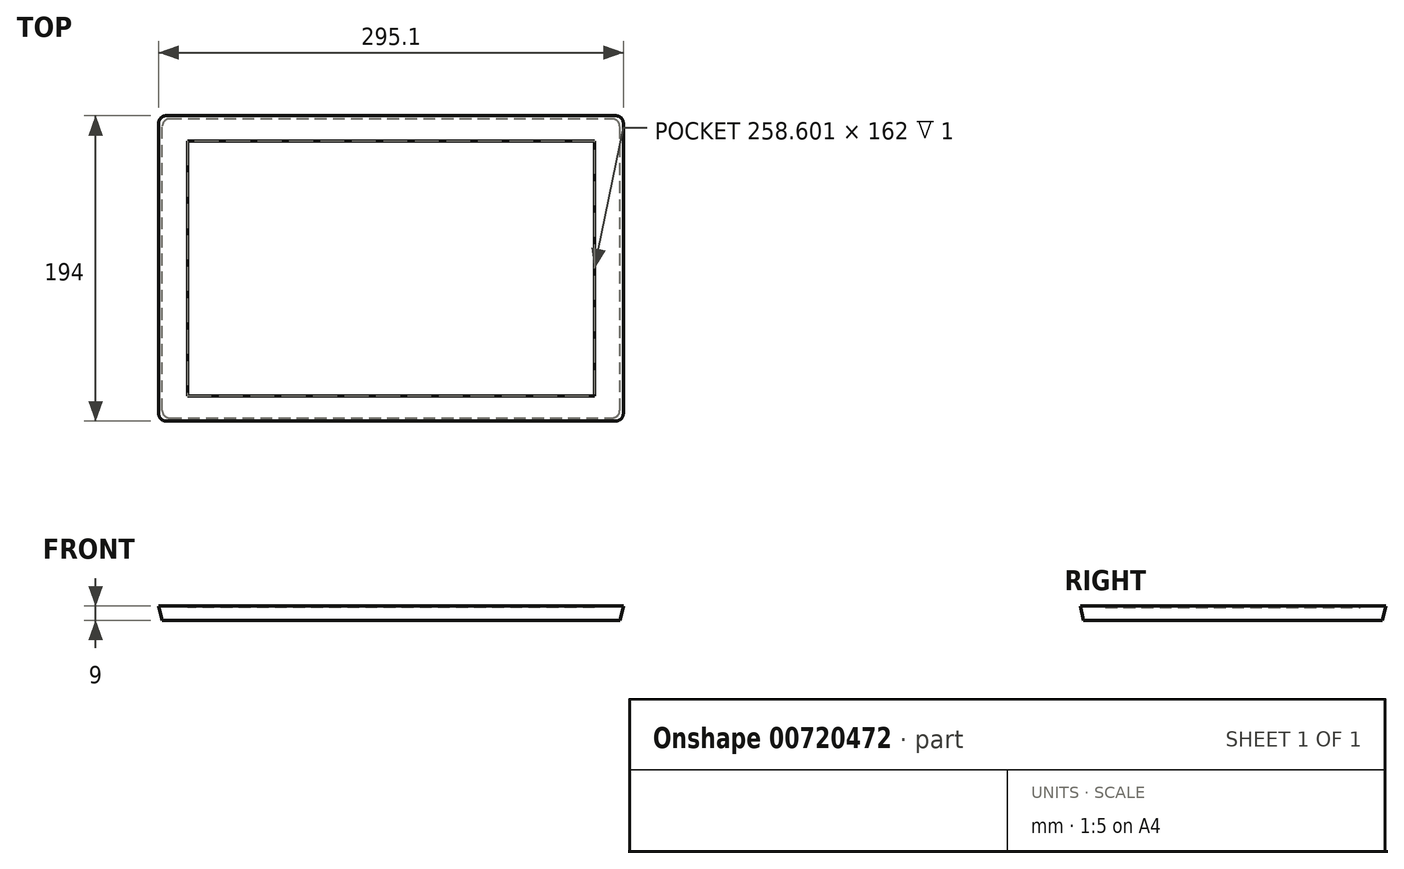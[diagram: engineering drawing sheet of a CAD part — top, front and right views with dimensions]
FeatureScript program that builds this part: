
annotation { "Feature Type Name" : "Feature", "Feature Type Description" : "" }
export const myFeature = defineFeature(function(context is Context, id is Id, definition is map)
    precondition{}
    {
        {
            var Q0;
            Q0=qCreatedBy(makeId("Top.planeOp"),FACE);
            var sketch = newSketch(context, id + "F0", { "sketchPlane" : qUnion([Q0])});
            skLineSegment(sketch, "E0.bottom", {"start": v(141, -97) * mm, "end": v(-141, -97) * mm});
            skLineSegment(sketch, "E0.top", {"start": v(141, 97) * mm, "end": v(-141, 97) * mm});
            skLineSegment(sketch, "E0.left", {"start": v(147.55, -92) * mm, "end": v(147.55, 99) * mm});
            skLineSegment(sketch, "E0.right", {"start": v(-147.55, -92) * mm, "end": v(-147.55, 99) * mm});
            skPoint(sketch, "E0.middle", {"position": v(0, 0) * mm});
            skLineSegment(sketch, "E1.bottom", {"start": v(138.75, -95) * mm, "end": v(-138.75, -95) * mm});
            skLineSegment(sketch, "E1.top", {"start": v(138.75, 95) * mm, "end": v(-138.75, 95) * mm});
            skLineSegment(sketch, "E1.left", {"start": v(145.3, -90) * mm, "end": v(145.3, 97) * mm});
            skLineSegment(sketch, "E1.right", {"start": v(-145.3, -90) * mm, "end": v(-145.3, 97) * mm});
            skLineSegment(sketch, "E2", {"start": v(-145.3, 95) * mm, "end": v(-145.3, 97) * mm});
            skLineSegment(sketch, "E3", {"start": v(-145.3, 95) * mm, "end": v(-138.75, 95) * mm});
            skLineSegment(sketch, "E4", {"start": v(-141, 97) * mm, "end": v(-147.55, 97) * mm});
            skLineSegment(sketch, "E5", {"start": v(-147.55, 99) * mm, "end": v(-147.55, 97) * mm});
            skLineSegment(sketch, "E6", {"start": v(-147.55, -92) * mm, "end": v(-147.55, -97) * mm});
            skLineSegment(sketch, "E7", {"start": v(-147.55, -97) * mm, "end": v(-141, -97) * mm});
            skLineSegment(sketch, "E8", {"start": v(-138.75, -95) * mm, "end": v(-145.3, -95) * mm});
            skLineSegment(sketch, "E9", {"start": v(-145.3, -95) * mm, "end": v(-145.3, -90) * mm});
            skLineSegment(sketch, "E10", {"start": v(141, -97) * mm, "end": v(147.55, -97) * mm});
            skLineSegment(sketch, "E11", {"start": v(147.55, -97) * mm, "end": v(147.55, -92) * mm});
            skLineSegment(sketch, "E12", {"start": v(145.3, -90) * mm, "end": v(145.3, -95) * mm});
            skLineSegment(sketch, "E13", {"start": v(145.3, -95) * mm, "end": v(138.75, -95) * mm});
            skLineSegment(sketch, "E14", {"start": v(138.75, 95) * mm, "end": v(145.3, 95) * mm});
            skLineSegment(sketch, "E15", {"start": v(145.3, 97) * mm, "end": v(145.3, 95) * mm});
            skLineSegment(sketch, "E16", {"start": v(141, 97) * mm, "end": v(147.55, 97) * mm});
            skLineSegment(sketch, "E17", {"start": v(147.55, 99) * mm, "end": v(147.55, 97) * mm});
            skLineSegment(sketch, "E18.bottom", {"start": v(129.3, -81) * mm, "end": v(-129.3, -81) * mm});
            skLineSegment(sketch, "E18.top", {"start": v(129.3, 81) * mm, "end": v(-129.3, 81) * mm});
            skLineSegment(sketch, "E18.left", {"start": v(129.3, -81) * mm, "end": v(129.3, 81) * mm});
            skLineSegment(sketch, "E18.right", {"start": v(-129.3, -81) * mm, "end": v(-129.3, 81) * mm});
            skSolve(sketch);
        }
        {
            var Q0;
            Q0=makeQuery(id+"F0.imprint","IMPRINT",FACE,{"disambiguationData":[TD([[makeQuery(id+"F0.imprint","IMPRINT",EDGE,{"derivedFrom":sQuery(id+"F0.wireOp",EDGE,"E1.bottom")}),-1.0]])]});
            var Q1;
            Q1=makeQuery(id+"F0.imprint","IMPRINT",FACE,{"disambiguationData":[TD([[makeQuery(id+"F0.imprint","IMPRINT",EDGE,{"derivedFrom":sQuery(id+"F0.wireOp",EDGE,"E0.bottom")}),-1.0]])]});
            var Q2;
            Q2=makeQuery(id+"F0.imprint","IMPRINT",FACE,{"disambiguationData":[TD([[makeQuery(id+"F0.imprint","IMPRINT",EDGE,{"derivedFrom":sQuery(id+"F0.wireOp",EDGE,"E18.bottom")}),-1.0]])]});
            extrude(context, id + "F1", {"entities" : qUnion([Q0, Q1, Q2]), "depth" : 9 * mm, "offsetDistance" : 25.4 * mm});
        }
        {
            var Q0;
            Q0=makeQuery(id+"F1.opExtrude","SWEPT_FACE",FACE,{"disambiguationData":[OSD([sQuery(id+"F0.wireOp",EDGE,"E0.left"),sQuery(id+"F0.wireOp",EDGE,"E11")])]});
            var sketch = newSketch(context, id + "F2", { "sketchPlane" : qUnion([Q0])});
            skPoint(sketch, "E19.0", {"position": v(-95, 0) * mm});
            skPoint(sketch, "E19.1", {"position": v(-97, 0) * mm});
            skPoint(sketch, "E19.2", {"position": v(-97, 9) * mm});
            skLineSegment(sketch, "E20", {"start": v(-95, 0) * mm, "end": v(-97, 9) * mm});
            skLineSegment(sketch, "E21", {"start": v(-97, 9) * mm, "end": v(-97, 0) * mm});
            skLineSegment(sketch, "E22", {"start": v(-97, 0) * mm, "end": v(-95, 0) * mm});
            skPoint(sketch, "E23.0", {"position": v(97, 0) * mm});
            skPoint(sketch, "E23.1", {"position": v(95, 0) * mm});
            skPoint(sketch, "E23.2", {"position": v(97, 9) * mm});
            skLineSegment(sketch, "E24", {"start": v(95, 0) * mm, "end": v(97, 9) * mm});
            skLineSegment(sketch, "E25", {"start": v(97, 9) * mm, "end": v(97, 0) * mm});
            skLineSegment(sketch, "E26", {"start": v(95, 0) * mm, "end": v(97, 0) * mm});
            skSolve(sketch);
        }
        {
            var Q0;
            Q0=makeQuery(id+"F2.imprint","IMPRINT",FACE,{"disambiguationData":[TD([[makeQuery(id+"F2.imprint","IMPRINT",EDGE,{"derivedFrom":sQuery(id+"F2.wireOp",EDGE,"E24")}),-1.0]])]});
            var Q1;
            Q1=makeQuery(id+"F2.imprint","IMPRINT",FACE,{"disambiguationData":[TD([[makeQuery(id+"F2.imprint","IMPRINT",EDGE,{"derivedFrom":sQuery(id+"F2.wireOp",EDGE,"E20")}),1.0]])]});
            extrude(context, id + "F3", {"entities" : qUnion([Q0, Q1]), "operationType" : NewBodyOperationType.REMOVE, "oppositeDirection" : true, "depth" : 330.2 * mm, "offsetDistance" : 25.4 * mm});
        }
        {
            var Q0;
            Q0=qCreatedBy(makeId("Front.planeOp"),FACE);
            var sketch = newSketch(context, id + "F4", { "sketchPlane" : qUnion([Q0])});
            skPoint(sketch, "E27.0", {"position": v(-145.3, 0) * mm});
            skPoint(sketch, "E27.1", {"position": v(-147.55, 0) * mm});
            skPoint(sketch, "E27.2", {"position": v(-147.55, 9) * mm});
            skLineSegment(sketch, "E28", {"start": v(-145.3, 0) * mm, "end": v(-147.55, 0) * mm});
            skLineSegment(sketch, "E29", {"start": v(-147.55, 0) * mm, "end": v(-147.55, 9) * mm});
            skLineSegment(sketch, "E30", {"start": v(-147.55, 9) * mm, "end": v(-145.3, 0) * mm});
            skPoint(sketch, "E31.0", {"position": v(147.55, 0) * mm});
            skPoint(sketch, "E31.1", {"position": v(145.3, 0) * mm});
            skPoint(sketch, "E31.2", {"position": v(147.55, 9) * mm});
            skLineSegment(sketch, "E32", {"start": v(145.3, 0) * mm, "end": v(147.55, 0) * mm});
            skLineSegment(sketch, "E33", {"start": v(147.55, 0) * mm, "end": v(147.55, 9) * mm});
            skLineSegment(sketch, "E34", {"start": v(147.55, 9) * mm, "end": v(145.3, 0) * mm});
            skSolve(sketch);
        }
        {
            var Q0;
            Q0=makeQuery(id+"F4.imprint","IMPRINT",FACE,{"disambiguationData":[TD([[makeQuery(id+"F4.imprint","IMPRINT",EDGE,{"derivedFrom":sQuery(id+"F4.wireOp",EDGE,"E28")}),-1.0]])]});
            var Q1;
            Q1=makeQuery(id+"F4.imprint","IMPRINT",FACE,{"disambiguationData":[TD([[makeQuery(id+"F4.imprint","IMPRINT",EDGE,{"derivedFrom":sQuery(id+"F4.wireOp",EDGE,"E32")}),1.0]])]});
            extrude(context, id + "F5", {"entities" : qUnion([Q0, Q1]), "operationType" : NewBodyOperationType.REMOVE, "endBound" : BoundingType.SYMMETRIC, "depth" : 381 * mm, "offsetDistance" : 25.4 * mm});
        }
        {
            var Q0;
            Q0=makeQuery(id+"F5.boolean.opBoolean","INTERSECT",EDGE,{"derivedFrom":[makeQuery(id+"F3.boolean.opBoolean","COPY",FACE,{"derivedFrom":makeQuery(id+"F3.opExtrude","SWEPT_FACE",FACE,{"disambiguationData":[OSD([sQuery(id+"F2.wireOp",EDGE,"E20")])]})}),makeQuery(id+"F5.opExtrude","SWEPT_FACE",FACE,{"disambiguationData":[OSD([sQuery(id+"F4.wireOp",EDGE,"E34")])]})]});
            var Q1;
            Q1=makeQuery(id+"F5.boolean.opBoolean","INTERSECT",EDGE,{"derivedFrom":[makeQuery(id+"F3.boolean.opBoolean","COPY",FACE,{"derivedFrom":makeQuery(id+"F3.opExtrude","SWEPT_FACE",FACE,{"disambiguationData":[OSD([sQuery(id+"F2.wireOp",EDGE,"E20")])]})}),makeQuery(id+"F5.opExtrude","SWEPT_FACE",FACE,{"disambiguationData":[OSD([sQuery(id+"F4.wireOp",EDGE,"E30")])]})]});
            var Q2;
            Q2=makeQuery(id+"F5.boolean.opBoolean","INTERSECT",EDGE,{"derivedFrom":[makeQuery(id+"F3.boolean.opBoolean","COPY",FACE,{"derivedFrom":makeQuery(id+"F3.opExtrude","SWEPT_FACE",FACE,{"disambiguationData":[OSD([sQuery(id+"F2.wireOp",EDGE,"E24")])]})}),makeQuery(id+"F5.opExtrude","SWEPT_FACE",FACE,{"disambiguationData":[OSD([sQuery(id+"F4.wireOp",EDGE,"E34")])]})]});
            var Q3;
            Q3=makeQuery(id+"F5.boolean.opBoolean","INTERSECT",EDGE,{"derivedFrom":[makeQuery(id+"F3.boolean.opBoolean","COPY",FACE,{"derivedFrom":makeQuery(id+"F3.opExtrude","SWEPT_FACE",FACE,{"disambiguationData":[OSD([sQuery(id+"F2.wireOp",EDGE,"E24")])]})}),makeQuery(id+"F5.opExtrude","SWEPT_FACE",FACE,{"disambiguationData":[OSD([sQuery(id+"F4.wireOp",EDGE,"E30")])]})]});
            fillet(context, id + "F6", {"entities" : qUnion([Q0, Q1, Q2, Q3]), "radius" : 5 * mm, "tangentPropagation" : true, "allowEdgeOverflow" : false});
        }
        {
            var Q0;
            Q0=makeQuery(id+"F0.imprint","IMPRINT",FACE,{"disambiguationData":[TD([[makeQuery(id+"F0.imprint","IMPRINT",EDGE,{"derivedFrom":sQuery(id+"F0.wireOp",EDGE,"E18.bottom")}),-1.0]])]});
            extrude(context, id + "F7", {"entities" : qUnion([Q0]), "operationType" : NewBodyOperationType.REMOVE, "depth" : 10 * mm, "offsetDistance" : 25.4 * mm, "hasSecondDirection" : true, "secondDirectionOppositeDirection" : false, "secondDirectionDepth" : 8 * mm});
        }
    });
